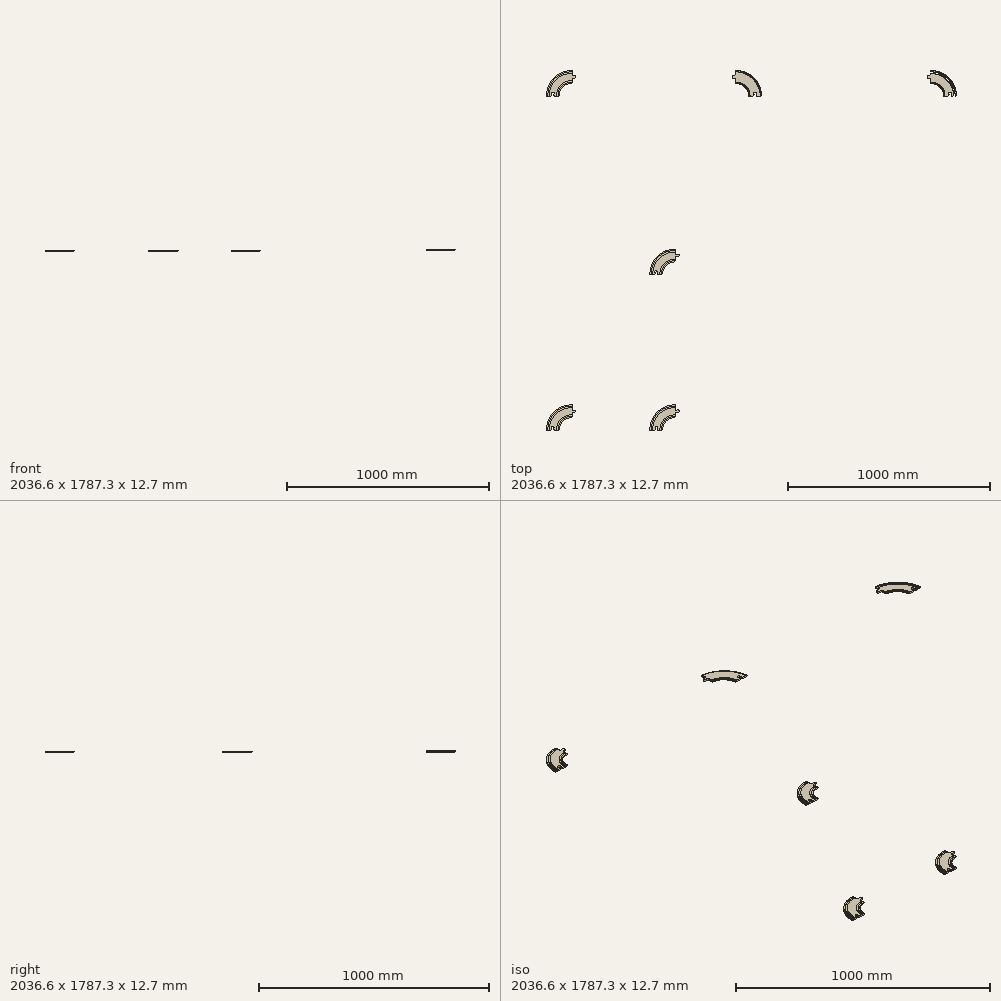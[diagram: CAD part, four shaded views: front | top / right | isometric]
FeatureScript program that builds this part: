
annotation { "Feature Type Name" : "Feature", "Feature Type Description" : "" }
export const myFeature = defineFeature(function(context is Context, id is Id, definition is map)
    precondition{}
    {
        {
            var Q0;
            Q0=qCreatedBy(makeId("Top.planeOp"),FACE);
            var sketch = newSketch(context, id + "F0", { "sketchPlane" : qUnion([Q0])});
            skArc(sketch, "E0", {"start": v(0, 127) * mm, "mid": v(-89.8, 89.8) * mm, "end": v(-127, 0) * mm});
            skArc(sketch, "E1.0", {"start": v(0, 63.5) * mm, "mid": v(-44.9, 44.9) * mm, "end": v(-63.5, 0) * mm});
            skLineSegment(sketch, "E2", {"start": v(-127, 0) * mm, "end": v(-101.6, 0) * mm});
            skLineSegment(sketch, "E3", {"start": v(0, 63.5) * mm, "end": v(0, 88.9) * mm});
            skArc(sketch, "E4", {"start": v(12.7, 88.9) * mm, "mid": v(19.05, 95.25) * mm, "end": v(12.7, 101.6) * mm});
            skPoint(sketch, "E5.start.orphan", {"position": v(12.7, 62.67) * mm});
            skArc(sketch, "E6", {"start": v(12.7, 88.9) * mm, "mid": v(6.35, 90.29) * mm, "end": v(0, 88.9) * mm});
            skArc(sketch, "E7.MirrorCS", {"start": v(12.7, 101.6) * mm, "mid": v(6.35, 100.21) * mm, "end": v(0, 101.6) * mm});
            skArc(sketch, "E8", {"start": v(-88.9, 12.7) * mm, "mid": v(-95.25, 19.05) * mm, "end": v(-101.6, 12.7) * mm});
            skLineSegment(sketch, "E9", {"start": v(-101.6, 12.7) * mm, "end": v(-102.39, 12.7) * mm});
            skPoint(sketch, "E10.startSnap0", {"position": v(-102.39, 12.7) * mm});
            skPoint(sketch, "E11.orphan", {"position": v(-71.93, 12.7) * mm});
            skLineSegment(sketch, "E12.trimOffspring", {"start": v(-126.36, 12.7) * mm, "end": v(-132.85, 12.7) * mm});
            skArc(sketch, "E13", {"start": v(-88.9, 12.7) * mm, "mid": v(-90.29, 6.35) * mm, "end": v(-88.9, 0) * mm});
            skArc(sketch, "E14.MirrorCS", {"start": v(-101.6, 12.7) * mm, "mid": v(-100.21, 6.35) * mm, "end": v(-101.6, 0) * mm});
            skPoint(sketch, "E10.end.orphan", {"position": v(-101.6, 0) * mm});
            skLineSegment(sketch, "E15.trimOffspring", {"start": v(0, 101.6) * mm, "end": v(0, 127) * mm});
            skLineSegment(sketch, "E16.trimOffspring", {"start": v(-88.9, 0) * mm, "end": v(-63.5, 0) * mm});
            skLineSegment(sketch, "E17", {"start": v(76.77, 161.45) * mm, "end": v(76.77, -32.66) * mm});
            skLineSegment(sketch, "E18", {"start": v(333.5, 184.4) * mm, "end": v(333.5, -54.92) * mm});
            skLineSegment(sketch, "E19.MirrorCS", {"start": v(411.86, 12.7) * mm, "end": v(411.07, 12.7) * mm});
            skArc(sketch, "E20.MirrorCS", {"start": v(526.16, 88.9) * mm, "mid": v(519.8, 90.29) * mm, "end": v(513.46, 88.9) * mm});
            skArc(sketch, "E21.MirrorCS", {"start": v(526.16, 101.6) * mm, "mid": v(519.8, 100.21) * mm, "end": v(513.46, 101.6) * mm});
            skArc(sketch, "E22.MirrorCS", {"start": v(411.86, 12.7) * mm, "mid": v(413.24, 6.35) * mm, "end": v(411.86, 0) * mm});
            skArc(sketch, "E23.MirrorCS", {"start": v(424.56, 12.7) * mm, "mid": v(418.2, 19.05) * mm, "end": v(411.86, 12.7) * mm});
            skArc(sketch, "E24.MirrorCS", {"start": v(526.16, 88.9) * mm, "mid": v(532.5, 95.25) * mm, "end": v(526.16, 101.6) * mm});
            skLineSegment(sketch, "E25.MirrorCS", {"start": v(513.46, 63.5) * mm, "end": v(513.46, 88.9) * mm});
            skArc(sketch, "E26.MirrorCS", {"start": v(424.56, 12.7) * mm, "mid": v(423.17, 6.35) * mm, "end": v(424.56, 0) * mm});
            skLineSegment(sketch, "E27.MirrorCS", {"start": v(513.46, 101.6) * mm, "end": v(513.46, 127) * mm});
            skLineSegment(sketch, "E28.MirrorCS", {"start": v(424.56, 0) * mm, "end": v(449.96, 0) * mm});
            skPoint(sketch, "E29.MirrorP", {"position": v(526.16, 62.67) * mm});
            skLineSegment(sketch, "E30.MirrorCS", {"start": v(387.1, 12.7) * mm, "end": v(380.6, 12.7) * mm});
            skLineSegment(sketch, "E31.MirrorCS", {"start": v(386.46, 0) * mm, "end": v(411.86, 0) * mm});
            skPoint(sketch, "E32.MirrorP", {"position": v(411.07, 12.7) * mm});
            skArc(sketch, "E33.MirrorCS", {"start": v(513.46, 127) * mm, "mid": v(423.65, 89.8) * mm, "end": v(386.46, 0) * mm});
            skPoint(sketch, "E34.MirrorP", {"position": v(411.86, 0) * mm});
            skArc(sketch, "E35.MirrorCS", {"start": v(513.46, 63.5) * mm, "mid": v(468.55, 44.9) * mm, "end": v(449.96, 0) * mm});
            skPoint(sketch, "E36.MirrorP", {"position": v(441.53, 12.7) * mm});
            skLineSegment(sketch, "E37.MirrorCS", {"start": v(-101.6, -874.4) * mm, "end": v(-102.39, -874.4) * mm});
            skLineSegment(sketch, "E38.MirrorCS", {"start": v(411.86, -874.4) * mm, "end": v(411.07, -874.4) * mm});
            skArc(sketch, "E39.MirrorCS", {"start": v(424.56, -874.4) * mm, "mid": v(423.17, -880.75) * mm, "end": v(424.56, -887.1) * mm});
            skArc(sketch, "E40.MirrorCS", {"start": v(526.16, -785.5) * mm, "mid": v(519.8, -786.88) * mm, "end": v(513.46, -785.5) * mm});
            skArc(sketch, "E41.MirrorCS", {"start": v(-101.6, -874.4) * mm, "mid": v(-100.21, -880.75) * mm, "end": v(-101.6, -887.1) * mm});
            skArc(sketch, "E42.MirrorCS", {"start": v(424.56, -874.4) * mm, "mid": v(418.2, -868.05) * mm, "end": v(411.86, -874.4) * mm});
            skArc(sketch, "E43.MirrorCS", {"start": v(526.16, -798.2) * mm, "mid": v(519.8, -796.81) * mm, "end": v(513.46, -798.2) * mm});
            skArc(sketch, "E44.MirrorCS", {"start": v(411.86, -874.4) * mm, "mid": v(413.24, -880.75) * mm, "end": v(411.86, -887.1) * mm});
            skArc(sketch, "E45.MirrorCS", {"start": v(-88.9, -874.4) * mm, "mid": v(-90.29, -880.75) * mm, "end": v(-88.9, -887.1) * mm});
            skArc(sketch, "E46.MirrorCS", {"start": v(-88.9, -874.4) * mm, "mid": v(-95.25, -868.05) * mm, "end": v(-101.6, -874.4) * mm});
            skLineSegment(sketch, "E47.MirrorCS", {"start": v(424.56, -887.1) * mm, "end": v(449.96, -887.1) * mm});
            skArc(sketch, "E48.MirrorCS", {"start": v(526.16, -798.2) * mm, "mid": v(532.5, -791.85) * mm, "end": v(526.16, -785.5) * mm});
            skArc(sketch, "E49.MirrorCS", {"start": v(12.7, -798.2) * mm, "mid": v(19.05, -791.85) * mm, "end": v(12.7, -785.5) * mm});
            skArc(sketch, "E50.MirrorCS", {"start": v(12.7, -785.5) * mm, "mid": v(6.35, -786.88) * mm, "end": v(0, -785.5) * mm});
            skArc(sketch, "E51.MirrorCS", {"start": v(12.7, -798.2) * mm, "mid": v(6.35, -796.81) * mm, "end": v(0, -798.2) * mm});
            skLineSegment(sketch, "E52.MirrorCS", {"start": v(-127, -887.1) * mm, "end": v(-101.6, -887.1) * mm});
            skLineSegment(sketch, "E53.MirrorCS", {"start": v(-88.9, -887.1) * mm, "end": v(-63.5, -887.1) * mm});
            skLineSegment(sketch, "E54.MirrorCS", {"start": v(-126.36, -874.4) * mm, "end": v(-132.85, -874.4) * mm});
            skLineSegment(sketch, "E55.MirrorCS", {"start": v(513.46, -823.6) * mm, "end": v(513.46, -798.2) * mm});
            skLineSegment(sketch, "E56.MirrorCS", {"start": v(387.1, -874.4) * mm, "end": v(380.6, -874.4) * mm});
            skLineSegment(sketch, "E57.MirrorCS", {"start": v(513.46, -785.5) * mm, "end": v(513.46, -760.1) * mm});
            skLineSegment(sketch, "E58.MirrorCS", {"start": v(0, -785.5) * mm, "end": v(0, -760.1) * mm});
            skLineSegment(sketch, "E59.MirrorCS", {"start": v(0, -823.6) * mm, "end": v(0, -798.2) * mm});
            skLineSegment(sketch, "E60.MirrorCS", {"start": v(386.46, -887.1) * mm, "end": v(411.86, -887.1) * mm});
            skPoint(sketch, "E61.MirrorP", {"position": v(526.16, -824.42) * mm});
            skPoint(sketch, "E62.MirrorP", {"position": v(-71.93, -874.4) * mm});
            skPoint(sketch, "E63.MirrorP", {"position": v(-101.6, -887.1) * mm});
            skArc(sketch, "E64.MirrorCS", {"start": v(0, -823.6) * mm, "mid": v(-44.9, -842.2) * mm, "end": v(-63.5, -887.1) * mm});
            skLineSegment(sketch, "E65.MirrorCS", {"start": v(333.5, -702.69) * mm, "end": v(333.5, -942.02) * mm});
            skArc(sketch, "E66.MirrorCS", {"start": v(513.46, -823.6) * mm, "mid": v(468.55, -842.2) * mm, "end": v(449.96, -887.1) * mm});
            skArc(sketch, "E67.MirrorCS", {"start": v(513.46, -760.1) * mm, "mid": v(423.65, -797.3) * mm, "end": v(386.46, -887.1) * mm});
            skPoint(sketch, "E68.MirrorP", {"position": v(411.86, -887.1) * mm});
            skPoint(sketch, "E69.MirrorP", {"position": v(441.53, -874.4) * mm});
            skArc(sketch, "E70.MirrorCS", {"start": v(0, -760.1) * mm, "mid": v(-89.8, -797.3) * mm, "end": v(-127, -887.1) * mm});
            skPoint(sketch, "E71.MirrorP", {"position": v(12.7, -824.42) * mm});
            skPoint(sketch, "E72.MirrorP", {"position": v(-102.39, -874.4) * mm});
            skLineSegment(sketch, "E73.MirrorCS", {"start": v(76.77, -725.65) * mm, "end": v(76.77, -919.76) * mm});
            skPoint(sketch, "E74.MirrorP", {"position": v(411.07, -874.4) * mm});
            skLineSegment(sketch, "E75.MirrorCS", {"start": v(411.86, -1647.6) * mm, "end": v(411.07, -1647.6) * mm});
            skArc(sketch, "E76.MirrorCS", {"start": v(424.56, -1647.6) * mm, "mid": v(418.2, -1641.26) * mm, "end": v(411.86, -1647.6) * mm});
            skArc(sketch, "E77.MirrorCS", {"start": v(424.56, -1647.6) * mm, "mid": v(423.17, -1653.96) * mm, "end": v(424.56, -1660.3) * mm});
            skArc(sketch, "E78.MirrorCS", {"start": v(411.86, -1647.6) * mm, "mid": v(413.24, -1653.96) * mm, "end": v(411.86, -1660.3) * mm});
            skLineSegment(sketch, "E79.MirrorCS", {"start": v(386.46, -1660.3) * mm, "end": v(411.86, -1660.3) * mm});
            skArc(sketch, "E80.MirrorCS", {"start": v(-88.9, -1647.6) * mm, "mid": v(-90.29, -1653.96) * mm, "end": v(-88.9, -1660.3) * mm});
            skLineSegment(sketch, "E81.MirrorCS", {"start": v(-127, -1660.3) * mm, "end": v(-101.6, -1660.3) * mm});
            skLineSegment(sketch, "E82.MirrorCS", {"start": v(-101.6, -1647.6) * mm, "end": v(-102.39, -1647.6) * mm});
            skArc(sketch, "E83.MirrorCS", {"start": v(-101.6, -1647.6) * mm, "mid": v(-100.21, -1653.96) * mm, "end": v(-101.6, -1660.3) * mm});
            skArc(sketch, "E84.MirrorCS", {"start": v(-88.9, -1647.6) * mm, "mid": v(-95.25, -1641.26) * mm, "end": v(-101.6, -1647.6) * mm});
            skArc(sketch, "E85.MirrorCS", {"start": v(526.16, -1571.4) * mm, "mid": v(519.8, -1570.02) * mm, "end": v(513.46, -1571.4) * mm});
            skArc(sketch, "E86.MirrorCS", {"start": v(526.16, -1558.7) * mm, "mid": v(519.8, -1560.1) * mm, "end": v(513.46, -1558.7) * mm});
            skLineSegment(sketch, "E87.MirrorCS", {"start": v(513.46, -1596.8) * mm, "end": v(513.46, -1571.4) * mm});
            skArc(sketch, "E88.MirrorCS", {"start": v(526.16, -1571.4) * mm, "mid": v(532.5, -1565.06) * mm, "end": v(526.16, -1558.7) * mm});
            skArc(sketch, "E89.MirrorCS", {"start": v(12.7, -1571.4) * mm, "mid": v(19.05, -1565.06) * mm, "end": v(12.7, -1558.7) * mm});
            skArc(sketch, "E90.MirrorCS", {"start": v(12.7, -1571.4) * mm, "mid": v(6.35, -1570.02) * mm, "end": v(0, -1571.4) * mm});
            skArc(sketch, "E91.MirrorCS", {"start": v(12.7, -1558.7) * mm, "mid": v(6.35, -1560.1) * mm, "end": v(0, -1558.7) * mm});
            skLineSegment(sketch, "E92.MirrorCS", {"start": v(-88.9, -1660.3) * mm, "end": v(-63.5, -1660.3) * mm});
            skLineSegment(sketch, "E93.MirrorCS", {"start": v(424.56, -1660.3) * mm, "end": v(449.96, -1660.3) * mm});
            skLineSegment(sketch, "E94.MirrorCS", {"start": v(513.46, -1558.7) * mm, "end": v(513.46, -1533.3) * mm});
            skLineSegment(sketch, "E95.MirrorCS", {"start": v(0, -1596.8) * mm, "end": v(0, -1571.4) * mm});
            skLineSegment(sketch, "E96.MirrorCS", {"start": v(-126.36, -1647.6) * mm, "end": v(-132.85, -1647.6) * mm});
            skLineSegment(sketch, "E97.MirrorCS", {"start": v(387.1, -1647.6) * mm, "end": v(380.6, -1647.6) * mm});
            skLineSegment(sketch, "E98.MirrorCS", {"start": v(0, -1558.7) * mm, "end": v(0, -1533.3) * mm});
            skPoint(sketch, "E99.MirrorP", {"position": v(526.16, -1597.64) * mm});
            skArc(sketch, "E100.MirrorCS", {"start": v(0, -1533.3) * mm, "mid": v(-89.8, -1570.5) * mm, "end": v(-127, -1660.3) * mm});
            skPoint(sketch, "E101.MirrorP", {"position": v(441.53, -1647.6) * mm});
            skArc(sketch, "E102.MirrorCS", {"start": v(513.46, -1596.8) * mm, "mid": v(468.55, -1615.4) * mm, "end": v(449.96, -1660.3) * mm});
            skPoint(sketch, "E103.MirrorP", {"position": v(411.07, -1647.6) * mm});
            skPoint(sketch, "E104.MirrorP", {"position": v(411.86, -1660.3) * mm});
            skPoint(sketch, "E105.MirrorP", {"position": v(-71.93, -1647.6) * mm});
            skPoint(sketch, "E106.MirrorP", {"position": v(-102.39, -1647.6) * mm});
            skLineSegment(sketch, "E107.MirrorCS", {"start": v(333.5, -1475.9) * mm, "end": v(333.5, -1715.23) * mm});
            skPoint(sketch, "E108.MirrorP", {"position": v(-101.6, -1660.3) * mm});
            skArc(sketch, "E109.MirrorCS", {"start": v(513.46, -1533.3) * mm, "mid": v(423.65, -1570.5) * mm, "end": v(386.46, -1660.3) * mm});
            skLineSegment(sketch, "E110.MirrorCS", {"start": v(76.77, -1498.86) * mm, "end": v(76.77, -1692.97) * mm});
            skPoint(sketch, "E111.MirrorP", {"position": v(12.7, -1597.64) * mm});
            skArc(sketch, "E112.MirrorCS", {"start": v(0, -1596.8) * mm, "mid": v(-44.9, -1615.4) * mm, "end": v(-63.5, -1660.3) * mm});
            skLineSegment(sketch, "E113", {"start": v(663.76, 185.94) * mm, "end": v(663.76, -109.84) * mm});
            skLineSegment(sketch, "E114", {"start": v(308.83, -128.2) * mm, "end": v(873.87, -128.2) * mm});
            skArc(sketch, "E115.MirrorCS", {"start": v(915.67, 12.7) * mm, "mid": v(914.28, 6.35) * mm, "end": v(915.67, 0) * mm});
            skArc(sketch, "E116.MirrorCS", {"start": v(902.97, 12.7) * mm, "mid": v(909.32, 19.05) * mm, "end": v(915.67, 12.7) * mm});
            skArc(sketch, "E117.MirrorCS", {"start": v(902.97, 12.7) * mm, "mid": v(904.35, 6.35) * mm, "end": v(902.97, 0) * mm});
            skLineSegment(sketch, "E118.MirrorCS", {"start": v(915.67, 12.7) * mm, "end": v(916.46, 12.7) * mm});
            skArc(sketch, "E119.MirrorCS", {"start": v(801.37, 88.9) * mm, "mid": v(807.72, 90.29) * mm, "end": v(814.07, 88.9) * mm});
            skArc(sketch, "E120.MirrorCS", {"start": v(801.37, 101.6) * mm, "mid": v(807.72, 100.21) * mm, "end": v(814.07, 101.6) * mm});
            skLineSegment(sketch, "E121.MirrorCS", {"start": v(814.07, 63.5) * mm, "end": v(814.07, 88.9) * mm});
            skArc(sketch, "E122.MirrorCS", {"start": v(801.37, 88.9) * mm, "mid": v(795.02, 95.25) * mm, "end": v(801.37, 101.6) * mm});
            skLineSegment(sketch, "E123.MirrorCS", {"start": v(814.07, 101.6) * mm, "end": v(814.07, 127) * mm});
            skLineSegment(sketch, "E124.MirrorCS", {"start": v(941.07, 0) * mm, "end": v(915.67, 0) * mm});
            skLineSegment(sketch, "E125.MirrorCS", {"start": v(902.97, 0) * mm, "end": v(877.57, 0) * mm});
            skLineSegment(sketch, "E126.MirrorCS", {"start": v(940.43, 12.7) * mm, "end": v(946.92, 12.7) * mm});
            skPoint(sketch, "E127.MirrorP", {"position": v(801.37, 62.67) * mm});
            skPoint(sketch, "E128.MirrorP", {"position": v(916.46, 12.7) * mm});
            skArc(sketch, "E129.MirrorCS", {"start": v(814.07, 63.5) * mm, "mid": v(858.97, 44.9) * mm, "end": v(877.57, 0) * mm});
            skArc(sketch, "E130.MirrorCS", {"start": v(814.07, 127) * mm, "mid": v(903.87, 89.8) * mm, "end": v(941.07, 0) * mm});
            skPoint(sketch, "E131.MirrorP", {"position": v(915.67, 0) * mm});
            skPoint(sketch, "E132.MirrorP", {"position": v(886, 12.7) * mm});
            skArc(sketch, "E133.MirrorCS", {"start": v(424.56, -269.1) * mm, "mid": v(423.17, -262.75) * mm, "end": v(424.56, -256.4) * mm});
            skArc(sketch, "E134.MirrorCS", {"start": v(526.16, -345.3) * mm, "mid": v(519.8, -346.68) * mm, "end": v(513.46, -345.3) * mm});
            skArc(sketch, "E135.MirrorCS", {"start": v(411.86, -269.1) * mm, "mid": v(413.24, -262.75) * mm, "end": v(411.86, -256.4) * mm});
            skLineSegment(sketch, "E136.MirrorCS", {"start": v(411.86, -269.1) * mm, "end": v(411.07, -269.1) * mm});
            skArc(sketch, "E137.MirrorCS", {"start": v(526.16, -358) * mm, "mid": v(519.8, -356.61) * mm, "end": v(513.46, -358) * mm});
            skArc(sketch, "E138.MirrorCS", {"start": v(424.56, -269.1) * mm, "mid": v(418.2, -275.45) * mm, "end": v(411.86, -269.1) * mm});
            skArc(sketch, "E139.MirrorCS", {"start": v(526.16, -345.3) * mm, "mid": v(532.5, -351.65) * mm, "end": v(526.16, -358) * mm});
            skLineSegment(sketch, "E140.MirrorCS", {"start": v(424.56, -256.4) * mm, "end": v(449.96, -256.4) * mm});
            skLineSegment(sketch, "E141.MirrorCS", {"start": v(513.46, -319.9) * mm, "end": v(513.46, -345.3) * mm});
            skLineSegment(sketch, "E142.MirrorCS", {"start": v(387.1, -269.1) * mm, "end": v(380.6, -269.1) * mm});
            skLineSegment(sketch, "E143.MirrorCS", {"start": v(386.46, -256.4) * mm, "end": v(411.86, -256.4) * mm});
            skLineSegment(sketch, "E144.MirrorCS", {"start": v(513.46, -358) * mm, "end": v(513.46, -383.4) * mm});
            skPoint(sketch, "E145.MirrorP", {"position": v(526.16, -319.07) * mm});
            skArc(sketch, "E146.MirrorCS", {"start": v(513.46, -383.4) * mm, "mid": v(423.65, -346.2) * mm, "end": v(386.46, -256.4) * mm});
            skArc(sketch, "E147.MirrorCS", {"start": v(513.46, -319.9) * mm, "mid": v(468.55, -301.3) * mm, "end": v(449.96, -256.4) * mm});
            skPoint(sketch, "E148.MirrorP", {"position": v(411.86, -256.4) * mm});
            skPoint(sketch, "E149.MirrorP", {"position": v(441.53, -269.1) * mm});
            skPoint(sketch, "E150.MirrorP", {"position": v(411.07, -269.1) * mm});
            skSolve(sketch);
        }
        {
            var Q0;
            Q0=makeQuery(id+"F0.imprint","IMPRINT",FACE,{"disambiguationData":[TD([[makeQuery(id+"F0.imprint","IMPRINT",EDGE,{"derivedFrom":sQuery(id+"F0.wireOp",EDGE,"E1.0")}),-1.0]])]});
            var Q1;
            Q1=makeQuery(id+"F0.imprint","IMPRINT",FACE,{"disambiguationData":[TD([[makeQuery(id+"F0.imprint","IMPRINT",EDGE,{"derivedFrom":sQuery(id+"F0.wireOp",EDGE,"E22.MirrorCS")}),-1.0]])]});
            var Q2;
            Q2=makeQuery(id+"F0.imprint","IMPRINT",FACE,{"disambiguationData":[TD([[makeQuery(id+"F0.imprint","IMPRINT",EDGE,{"derivedFrom":sQuery(id+"F0.wireOp",EDGE,"E39.MirrorCS")}),1.0]])]});
            var Q3;
            Q3=makeQuery(id+"F0.imprint","IMPRINT",FACE,{"disambiguationData":[TD([[makeQuery(id+"F0.imprint","IMPRINT",EDGE,{"derivedFrom":sQuery(id+"F0.wireOp",EDGE,"E41.MirrorCS")}),-1.0]])]});
            var Q4;
            Q4=makeQuery(id+"F0.imprint","IMPRINT",FACE,{"disambiguationData":[TD([[makeQuery(id+"F0.imprint","IMPRINT",EDGE,{"derivedFrom":sQuery(id+"F0.wireOp",EDGE,"E80.MirrorCS")}),1.0]])]});
            var Q5;
            Q5=makeQuery(id+"F0.imprint","IMPRINT",FACE,{"disambiguationData":[TD([[makeQuery(id+"F0.imprint","IMPRINT",EDGE,{"derivedFrom":sQuery(id+"F0.wireOp",EDGE,"E115.MirrorCS")}),1.0]])]});
            var Q6;
            Q6=makeQuery(id+"F0.imprint","IMPRINT",FACE,{"disambiguationData":[TD([[makeQuery(id+"F0.imprint","IMPRINT",EDGE,{"derivedFrom":sQuery(id+"F0.wireOp",EDGE,"E133.MirrorCS")}),-1.0]])]});
            var Q7;
            Q7=makeQuery(id+"F0.imprint","IMPRINT",FACE,{"disambiguationData":[TD([[makeQuery(id+"F0.imprint","IMPRINT",EDGE,{"derivedFrom":sQuery(id+"F0.wireOp",EDGE,"E76.MirrorCS")}),-1.0]])]});
            extrude(context, id + "F1", {"entities" : qUnion([Q0, Q1, Q2, Q3, Q4, Q5, Q6, Q7]), "depth" : 6.35 * mm});
        }
        {
            var Q0;
            Q0=makeQuery(id+"F1.opExtrude","CAP_FACE",FACE,{"disambiguationData":[OSD([sQuery(id+"F0.wireOp",EDGE,"E0"),sQuery(id+"F0.wireOp",EDGE,"E1.0"),sQuery(id+"F0.wireOp",EDGE,"E2"),sQuery(id+"F0.wireOp",EDGE,"E3"),sQuery(id+"F0.wireOp",EDGE,"E4"),sQuery(id+"F0.wireOp",EDGE,"E6"),sQuery(id+"F0.wireOp",EDGE,"E7.MirrorCS"),sQuery(id+"F0.wireOp",EDGE,"E8"),sQuery(id+"F0.wireOp",EDGE,"E13"),sQuery(id+"F0.wireOp",EDGE,"E14.MirrorCS"),sQuery(id+"F0.wireOp",EDGE,"E15.trimOffspring"),sQuery(id+"F0.wireOp",EDGE,"E16.trimOffspring")])],"isStart":false});
            var sketch = newSketch(context, id + "F2", { "sketchPlane" : qUnion([Q0])});
            skArc(sketch, "E151.0", {"start": v(0, 63.5) * mm, "mid": v(-44.9, 44.9) * mm, "end": v(-63.5, 0) * mm});
            skArc(sketch, "E151.1", {"start": v(0, 127) * mm, "mid": v(-89.8, 89.8) * mm, "end": v(-127, 0) * mm});
            skLineSegment(sketch, "E152.0", {"start": v(76.77, 161.45) * mm, "end": v(76.77, -32.66) * mm});
            skLineSegment(sketch, "E152.1", {"start": v(333.5, 184.4) * mm, "end": v(333.5, -54.92) * mm});
            skArc(sketch, "E153.0", {"start": v(0, 69.85) * mm, "mid": v(-49.4, 49.4) * mm, "end": v(-69.85, 0) * mm});
            skArc(sketch, "E154.0", {"start": v(0, 77.47) * mm, "mid": v(-54.78, 54.78) * mm, "end": v(-77.47, 0) * mm});
            skArc(sketch, "E155.0", {"start": v(0, 120.65) * mm, "mid": v(-85.31, 85.31) * mm, "end": v(-120.65, 0) * mm});
            skArc(sketch, "E156.0", {"start": v(0, 113.03) * mm, "mid": v(-79.92, 79.92) * mm, "end": v(-113.03, 0) * mm});
            skArc(sketch, "E157.MirrorCS", {"start": v(153.53, 113.03) * mm, "mid": v(233.46, 79.92) * mm, "end": v(266.56, 0) * mm});
            skArc(sketch, "E158.MirrorCS", {"start": v(153.53, 120.65) * mm, "mid": v(238.85, 85.31) * mm, "end": v(274.18, 0) * mm});
            skArc(sketch, "E159.MirrorCS", {"start": v(153.53, 69.85) * mm, "mid": v(202.93, 49.4) * mm, "end": v(223.38, 0) * mm});
            skArc(sketch, "E160.MirrorCS", {"start": v(153.53, 77.47) * mm, "mid": v(208.31, 54.78) * mm, "end": v(231, 0) * mm});
            skArc(sketch, "E161.MirrorCS", {"start": v(513.46, 120.65) * mm, "mid": v(428.14, 85.31) * mm, "end": v(392.8, 0) * mm});
            skArc(sketch, "E162.MirrorCS", {"start": v(513.46, 113.03) * mm, "mid": v(433.53, 79.92) * mm, "end": v(400.43, 0) * mm});
            skArc(sketch, "E163.MirrorCS", {"start": v(513.46, 69.85) * mm, "mid": v(464.06, 49.4) * mm, "end": v(443.6, 0) * mm});
            skArc(sketch, "E164.MirrorCS", {"start": v(513.46, 77.47) * mm, "mid": v(458.68, 54.78) * mm, "end": v(435.99, 0) * mm});
            skArc(sketch, "E165.MirrorCS", {"start": v(0, -403.9) * mm, "mid": v(-54.78, -381.21) * mm, "end": v(-77.47, -326.43) * mm});
            skArc(sketch, "E166.MirrorCS", {"start": v(0, -396.28) * mm, "mid": v(-49.4, -375.82) * mm, "end": v(-69.85, -326.43) * mm});
            skArc(sketch, "E167.MirrorCS", {"start": v(0, -447.08) * mm, "mid": v(-85.31, -411.74) * mm, "end": v(-120.65, -326.43) * mm});
            skLineSegment(sketch, "E168.MirrorCS", {"start": v(333.5, -510.84) * mm, "end": v(333.5, -271.5) * mm});
            skArc(sketch, "E169.MirrorCS", {"start": v(0, -439.46) * mm, "mid": v(-79.92, -406.36) * mm, "end": v(-113.03, -326.43) * mm});
            skArc(sketch, "E170.MirrorCS", {"start": v(153.53, -439.46) * mm, "mid": v(233.46, -406.36) * mm, "end": v(266.56, -326.43) * mm});
            skLineSegment(sketch, "E171.MirrorCS", {"start": v(76.77, -487.88) * mm, "end": v(76.77, -293.77) * mm});
            skArc(sketch, "E172.MirrorCS", {"start": v(0, -453.43) * mm, "mid": v(-89.8, -416.23) * mm, "end": v(-127, -326.43) * mm});
            skArc(sketch, "E173.MirrorCS", {"start": v(153.53, -447.08) * mm, "mid": v(238.85, -411.74) * mm, "end": v(274.18, -326.43) * mm});
            skArc(sketch, "E174.MirrorCS", {"start": v(0, -389.93) * mm, "mid": v(-44.9, -371.33) * mm, "end": v(-63.5, -326.43) * mm});
            skArc(sketch, "E175.MirrorCS", {"start": v(513.46, -396.28) * mm, "mid": v(464.06, -375.82) * mm, "end": v(443.6, -326.43) * mm});
            skArc(sketch, "E176.MirrorCS", {"start": v(153.53, -396.28) * mm, "mid": v(202.93, -375.82) * mm, "end": v(223.38, -326.43) * mm});
            skArc(sketch, "E177.MirrorCS", {"start": v(153.53, -403.9) * mm, "mid": v(208.31, -381.21) * mm, "end": v(231, -326.43) * mm});
            skArc(sketch, "E178.MirrorCS", {"start": v(513.46, -439.46) * mm, "mid": v(433.53, -406.36) * mm, "end": v(400.43, -326.43) * mm});
            skArc(sketch, "E179.MirrorCS", {"start": v(513.46, -447.08) * mm, "mid": v(428.14, -411.74) * mm, "end": v(392.8, -326.43) * mm});
            skArc(sketch, "E180.MirrorCS", {"start": v(513.46, -403.9) * mm, "mid": v(458.68, -381.21) * mm, "end": v(435.99, -326.43) * mm});
            skLineSegment(sketch, "E181", {"start": v(-77.47, 0) * mm, "end": v(-69.85, 0) * mm});
            skLineSegment(sketch, "E182", {"start": v(-113.03, 0) * mm, "end": v(-120.65, 0) * mm});
            skLineSegment(sketch, "E183", {"start": v(0, 69.85) * mm, "end": v(0, 77.47) * mm});
            skLineSegment(sketch, "E184", {"start": v(0, 113.03) * mm, "end": v(0, 120.65) * mm});
            skLineSegment(sketch, "E185", {"start": v(153.53, 77.47) * mm, "end": v(153.53, 69.85) * mm});
            skLineSegment(sketch, "E186", {"start": v(153.53, 113.03) * mm, "end": v(153.53, 120.65) * mm});
            skLineSegment(sketch, "E187", {"start": v(223.38, 0) * mm, "end": v(231, 0) * mm});
            skLineSegment(sketch, "E188", {"start": v(266.56, 0) * mm, "end": v(274.18, 0) * mm});
            skLineSegment(sketch, "E189", {"start": v(392.8, 0) * mm, "end": v(400.43, 0) * mm});
            skLineSegment(sketch, "E190", {"start": v(435.99, 0) * mm, "end": v(443.6, 0) * mm});
            skLineSegment(sketch, "E191", {"start": v(513.46, 69.85) * mm, "end": v(513.46, 77.47) * mm});
            skLineSegment(sketch, "E192", {"start": v(513.46, 120.65) * mm, "end": v(513.46, 113.03) * mm});
            skLineSegment(sketch, "E193", {"start": v(392.8, -326.43) * mm, "end": v(400.43, -326.43) * mm});
            skLineSegment(sketch, "E194", {"start": v(435.99, -326.43) * mm, "end": v(443.6, -326.43) * mm});
            skLineSegment(sketch, "E195", {"start": v(513.46, -396.28) * mm, "end": v(513.46, -403.9) * mm});
            skLineSegment(sketch, "E196", {"start": v(513.46, -447.08) * mm, "end": v(513.46, -439.46) * mm});
            skLineSegment(sketch, "E197", {"start": v(266.56, -326.43) * mm, "end": v(274.18, -326.43) * mm});
            skLineSegment(sketch, "E198", {"start": v(231, -326.43) * mm, "end": v(223.38, -326.43) * mm});
            skLineSegment(sketch, "E199", {"start": v(153.53, -396.28) * mm, "end": v(153.53, -403.9) * mm});
            skLineSegment(sketch, "E200", {"start": v(153.53, -439.46) * mm, "end": v(153.53, -447.08) * mm});
            skLineSegment(sketch, "E201", {"start": v(0, -403.9) * mm, "end": v(0, -396.28) * mm});
            skLineSegment(sketch, "E202", {"start": v(0, -447.08) * mm, "end": v(0, -439.46) * mm});
            skLineSegment(sketch, "E203", {"start": v(-69.85, -326.43) * mm, "end": v(-77.47, -326.43) * mm});
            skLineSegment(sketch, "E204", {"start": v(-113.03, -326.43) * mm, "end": v(-120.65, -326.43) * mm});
            skArc(sketch, "E205.0", {"start": v(0, -760.1) * mm, "mid": v(-89.8, -797.3) * mm, "end": v(-127, -887.1) * mm});
            skArc(sketch, "E205.1", {"start": v(0, -823.6) * mm, "mid": v(-44.9, -842.2) * mm, "end": v(-63.5, -887.1) * mm});
            skArc(sketch, "E205.2", {"start": v(513.46, -760.1) * mm, "mid": v(423.65, -797.3) * mm, "end": v(386.46, -887.1) * mm});
            skArc(sketch, "E205.3", {"start": v(513.46, -823.6) * mm, "mid": v(468.55, -842.2) * mm, "end": v(449.96, -887.1) * mm});
            skPoint(sketch, "E206.endSnap0", {"position": v(0, -606.77) * mm});
            skLineSegment(sketch, "E207.MirrorCS", {"start": v(0, -766.45) * mm, "end": v(0, -774.07) * mm});
            skLineSegment(sketch, "E208.MirrorCS", {"start": v(392.8, -887.1) * mm, "end": v(400.43, -887.1) * mm});
            skLineSegment(sketch, "E209.MirrorCS", {"start": v(0, -809.63) * mm, "end": v(0, -817.25) * mm});
            skLineSegment(sketch, "E210.MirrorCS", {"start": v(435.99, -887.1) * mm, "end": v(443.6, -887.1) * mm});
            skLineSegment(sketch, "E211.MirrorCS", {"start": v(513.46, -817.25) * mm, "end": v(513.46, -809.63) * mm});
            skLineSegment(sketch, "E212.MirrorCS", {"start": v(513.46, -766.45) * mm, "end": v(513.46, -774.07) * mm});
            skLineSegment(sketch, "E213.MirrorCS", {"start": v(-69.85, -887.1) * mm, "end": v(-77.47, -887.1) * mm});
            skLineSegment(sketch, "E214.MirrorCS", {"start": v(231, -887.1) * mm, "end": v(223.38, -887.1) * mm});
            skLineSegment(sketch, "E215.MirrorCS", {"start": v(153.53, -774.07) * mm, "end": v(153.53, -766.45) * mm});
            skLineSegment(sketch, "E216.MirrorCS", {"start": v(153.53, -817.25) * mm, "end": v(153.53, -809.63) * mm});
            skLineSegment(sketch, "E217.MirrorCS", {"start": v(266.56, -887.1) * mm, "end": v(274.18, -887.1) * mm});
            skLineSegment(sketch, "E218.MirrorCS", {"start": v(-113.03, -887.1) * mm, "end": v(-120.65, -887.1) * mm});
            skLineSegment(sketch, "E219.MirrorCS", {"start": v(333.5, -702.69) * mm, "end": v(333.5, -942.02) * mm});
            skLineSegment(sketch, "E220.MirrorCS", {"start": v(0, -760.1) * mm, "end": v(0, -453.43) * mm});
            skArc(sketch, "E221.MirrorCS", {"start": v(0, -774.07) * mm, "mid": v(-79.92, -807.17) * mm, "end": v(-113.03, -887.1) * mm});
            skArc(sketch, "E222.MirrorCS", {"start": v(513.46, -766.45) * mm, "mid": v(428.14, -801.79) * mm, "end": v(392.8, -887.1) * mm});
            skArc(sketch, "E223.MirrorCS", {"start": v(153.53, -774.07) * mm, "mid": v(233.46, -807.17) * mm, "end": v(266.56, -887.1) * mm});
            skLineSegment(sketch, "E224.MirrorCS", {"start": v(76.77, -725.65) * mm, "end": v(76.77, -919.76) * mm});
            skArc(sketch, "E225.MirrorCS", {"start": v(153.53, -766.45) * mm, "mid": v(238.85, -801.79) * mm, "end": v(274.18, -887.1) * mm});
            skArc(sketch, "E226.MirrorCS", {"start": v(153.53, -809.63) * mm, "mid": v(208.31, -832.32) * mm, "end": v(231, -887.1) * mm});
            skArc(sketch, "E227.MirrorCS", {"start": v(513.46, -817.25) * mm, "mid": v(464.06, -837.7) * mm, "end": v(443.6, -887.1) * mm});
            skArc(sketch, "E228.MirrorCS", {"start": v(0, -766.45) * mm, "mid": v(-85.31, -801.79) * mm, "end": v(-120.65, -887.1) * mm});
            skArc(sketch, "E229.MirrorCS", {"start": v(0, -817.25) * mm, "mid": v(-49.4, -837.7) * mm, "end": v(-69.85, -887.1) * mm});
            skArc(sketch, "E230.MirrorCS", {"start": v(0, -809.63) * mm, "mid": v(-54.78, -832.32) * mm, "end": v(-77.47, -887.1) * mm});
            skArc(sketch, "E231.MirrorCS", {"start": v(513.46, -809.63) * mm, "mid": v(458.68, -832.32) * mm, "end": v(435.99, -887.1) * mm});
            skArc(sketch, "E232.MirrorCS", {"start": v(513.46, -774.07) * mm, "mid": v(433.53, -807.17) * mm, "end": v(400.43, -887.1) * mm});
            skArc(sketch, "E233.MirrorCS", {"start": v(153.53, -817.25) * mm, "mid": v(202.93, -837.7) * mm, "end": v(223.38, -887.1) * mm});
            skArc(sketch, "E234.0", {"start": v(0, -1533.3) * mm, "mid": v(-89.8, -1570.5) * mm, "end": v(-127, -1660.3) * mm});
            skArc(sketch, "E235.0", {"start": v(0, -1590.46) * mm, "mid": v(-49.4, -1610.92) * mm, "end": v(-69.85, -1660.3) * mm});
            skArc(sketch, "E236.0", {"start": v(0, -1582.84) * mm, "mid": v(-54.78, -1605.53) * mm, "end": v(-77.47, -1660.3) * mm});
            skArc(sketch, "E237.0", {"start": v(513.46, -1533.3) * mm, "mid": v(423.65, -1570.5) * mm, "end": v(386.46, -1660.3) * mm});
            skArc(sketch, "E238.0", {"start": v(513.46, -1590.46) * mm, "mid": v(464.06, -1610.92) * mm, "end": v(443.6, -1660.3) * mm});
            skArc(sketch, "E239.0", {"start": v(513.46, -1582.84) * mm, "mid": v(458.68, -1605.53) * mm, "end": v(435.99, -1660.3) * mm});
            skArc(sketch, "E240.0", {"start": v(513.46, -1539.66) * mm, "mid": v(428.14, -1575) * mm, "end": v(392.8, -1660.3) * mm});
            skArc(sketch, "E241.0", {"start": v(513.46, -1547.28) * mm, "mid": v(433.53, -1580.39) * mm, "end": v(400.43, -1660.3) * mm});
            skLineSegment(sketch, "E242.0", {"start": v(0, -1660.3) * mm, "end": v(0, -1660.3) * mm});
            skArc(sketch, "E243.0", {"start": v(0, -1539.66) * mm, "mid": v(-85.31, -1575) * mm, "end": v(-120.65, -1660.3) * mm});
            skArc(sketch, "E244.0", {"start": v(0, -1547.28) * mm, "mid": v(-79.92, -1580.39) * mm, "end": v(-113.03, -1660.3) * mm});
            skLineSegment(sketch, "E245", {"start": v(0, -1547.28) * mm, "end": v(0, -1539.66) * mm});
            skLineSegment(sketch, "E246", {"start": v(-77.47, -1660.3) * mm, "end": v(-69.85, -1660.3) * mm});
            skLineSegment(sketch, "E247", {"start": v(-113.03, -1660.3) * mm, "end": v(-120.65, -1660.3) * mm});
            skLineSegment(sketch, "E248", {"start": v(0, -1590.46) * mm, "end": v(0, -1582.84) * mm});
            skLineSegment(sketch, "E249", {"start": v(400.43, -1660.3) * mm, "end": v(392.8, -1660.3) * mm});
            skLineSegment(sketch, "E250", {"start": v(435.99, -1660.3) * mm, "end": v(443.6, -1660.3) * mm});
            skLineSegment(sketch, "E251", {"start": v(513.46, -1590.46) * mm, "end": v(513.46, -1582.84) * mm});
            skLineSegment(sketch, "E252", {"start": v(513.46, -1547.28) * mm, "end": v(513.46, -1539.66) * mm});
            skSolve(sketch);
        }
        {
            var Q0;
            Q0 = qSketchRegion(id + "F2", true);
            extrude(context, id + "F3", {"entities" : qUnion([Q0]), "operationType" : NewBodyOperationType.REMOVE, "oppositeDirection" : true, "depth" : 1.9 * mm});
        }
        {
            var Q0;
            Q0=makeQuery(id+"F1.opExtrude","CAP_FACE",FACE,{"disambiguationData":[OSD([sQuery(id+"F0.wireOp",EDGE,"E115.MirrorCS"),sQuery(id+"F0.wireOp",EDGE,"E116.MirrorCS"),sQuery(id+"F0.wireOp",EDGE,"E117.MirrorCS"),sQuery(id+"F0.wireOp",EDGE,"E121.MirrorCS"),sQuery(id+"F0.wireOp",EDGE,"E120.MirrorCS"),sQuery(id+"F0.wireOp",EDGE,"E122.MirrorCS"),sQuery(id+"F0.wireOp",EDGE,"E119.MirrorCS"),sQuery(id+"F0.wireOp",EDGE,"E123.MirrorCS"),sQuery(id+"F0.wireOp",EDGE,"E124.MirrorCS"),sQuery(id+"F0.wireOp",EDGE,"E125.MirrorCS"),sQuery(id+"F0.wireOp",EDGE,"E129.MirrorCS"),sQuery(id+"F0.wireOp",EDGE,"E130.MirrorCS")])],"isStart":false});
            var sketch = newSketch(context, id + "F4", { "sketchPlane" : qUnion([Q0])});
            skArc(sketch, "E253.0", {"start": v(814.07, 69.85) * mm, "mid": v(863.46, 49.4) * mm, "end": v(883.92, 0) * mm});
            skArc(sketch, "E254.0", {"start": v(814.07, 77.47) * mm, "mid": v(868.85, 54.78) * mm, "end": v(891.54, 0) * mm});
            skArc(sketch, "E255.0", {"start": v(814.07, 120.65) * mm, "mid": v(899.38, 85.31) * mm, "end": v(934.72, 0) * mm});
            skArc(sketch, "E256.0", {"start": v(814.07, 113.03) * mm, "mid": v(894, 79.92) * mm, "end": v(927.1, 0) * mm});
            skLineSegment(sketch, "E257", {"start": v(814.07, 120.65) * mm, "end": v(814.07, 113.03) * mm});
            skLineSegment(sketch, "E258", {"start": v(814.07, 77.47) * mm, "end": v(814.07, 69.85) * mm});
            skLineSegment(sketch, "E259", {"start": v(891.54, 0) * mm, "end": v(883.92, 0) * mm});
            skLineSegment(sketch, "E260", {"start": v(927.1, 0) * mm, "end": v(934.72, 0) * mm});
            skSolve(sketch);
        }
        {
            var Q0;
            Q0=makeQuery(id+"F4.imprint","IMPRINT",FACE,{"disambiguationData":[TD([[makeQuery(id+"F4.imprint","IMPRINT",EDGE,{"derivedFrom":sQuery(id+"F4.wireOp",EDGE,"E255.0")}),-1.0]])]});
            var Q1;
            Q1=makeQuery(id+"F4.imprint","IMPRINT",FACE,{"disambiguationData":[TD([[makeQuery(id+"F4.imprint","IMPRINT",EDGE,{"derivedFrom":sQuery(id+"F4.wireOp",EDGE,"E253.0")}),1.0]])]});
            extrude(context, id + "F5", {"entities" : qUnion([Q0, Q1]), "operationType" : NewBodyOperationType.REMOVE, "oppositeDirection" : true, "depth" : 1.9 * mm});
        }
        {
            var Q0;
            {var subQ0=sQuery(id+"F0.wireOp",EDGE,"E125.MirrorCS");var subQ1=sQuery(id+"F0.wireOp",EDGE,"E123.MirrorCS");var subQ2=sQuery(id+"F0.wireOp",EDGE,"E119.MirrorCS");var subQ3=sQuery(id+"F0.wireOp",EDGE,"E122.MirrorCS");var subQ4=sQuery(id+"F0.wireOp",EDGE,"E115.MirrorCS");var subQ5=sQuery(id+"F0.wireOp",EDGE,"E120.MirrorCS");var subQ6=sQuery(id+"F0.wireOp",EDGE,"E116.MirrorCS");var subQ7=sQuery(id+"F0.wireOp",EDGE,"E117.MirrorCS");var subQ8=sQuery(id+"F0.wireOp",EDGE,"E124.MirrorCS");var subQ9=sQuery(id+"F0.wireOp",EDGE,"E121.MirrorCS");Q0=makeQuery(id+"F5.boolean.opBoolean","SPLIT",FACE,{"disambiguationData":[TD([makeQuery(id+"F1.opExtrude","SWEPT_FACE",FACE,{"disambiguationData":[OSD([subQ4])]})])],"derivedFrom":makeQuery(id+"F1.opExtrude","CAP_FACE",FACE,{"disambiguationData":[OSD([subQ4,subQ6,subQ7,subQ9,subQ5,subQ3,subQ2,subQ1,subQ8,subQ0,sQuery(id+"F0.wireOp",EDGE,"E129.MirrorCS"),sQuery(id+"F0.wireOp",EDGE,"E130.MirrorCS")])],"isStart":false})});}
            var sketch = newSketch(context, id + "F6", { "sketchPlane" : qUnion([Q0])});
            skLineSegment(sketch, "E261", {"start": v(1034.93, 198.47) * mm, "end": v(1034.93, -110.58) * mm});
            skPoint(sketch, "E262.0", {"position": v(916.46, 12.7) * mm});
            skArc(sketch, "E262.1", {"start": v(814.07, 120.65) * mm, "mid": v(899.38, 85.31) * mm, "end": v(934.72, 0) * mm});
            skArc(sketch, "E262.2", {"start": v(814.07, 113.03) * mm, "mid": v(894, 79.92) * mm, "end": v(927.1, 0) * mm});
            skArc(sketch, "E262.3", {"start": v(814.07, 127) * mm, "mid": v(903.87, 89.8) * mm, "end": v(941.07, 0) * mm});
            skLineSegment(sketch, "E262.4", {"start": v(941.07, 0) * mm, "end": v(915.67, 0) * mm});
            skLineSegment(sketch, "E262.5", {"start": v(902.97, 0) * mm, "end": v(877.57, 0) * mm});
            skArc(sketch, "E262.6", {"start": v(902.97, 12.7) * mm, "mid": v(904.35, 6.35) * mm, "end": v(902.97, 0) * mm});
            skArc(sketch, "E262.7", {"start": v(902.97, 12.7) * mm, "mid": v(909.32, 19.05) * mm, "end": v(915.67, 12.7) * mm});
            skArc(sketch, "E262.8", {"start": v(915.67, 12.7) * mm, "mid": v(914.28, 6.35) * mm, "end": v(915.67, 0) * mm});
            skPoint(sketch, "E262.9", {"position": v(886, 12.7) * mm});
            skArc(sketch, "E262.10", {"start": v(814.07, 77.47) * mm, "mid": v(868.85, 54.78) * mm, "end": v(891.54, 0) * mm});
            skArc(sketch, "E262.11", {"start": v(814.07, 69.85) * mm, "mid": v(863.46, 49.4) * mm, "end": v(883.92, 0) * mm});
            skArc(sketch, "E262.12", {"start": v(814.07, 63.5) * mm, "mid": v(858.97, 44.9) * mm, "end": v(877.57, 0) * mm});
            skLineSegment(sketch, "E262.13", {"start": v(814.07, 63.5) * mm, "end": v(814.07, 88.9) * mm});
            skLineSegment(sketch, "E262.14", {"start": v(814.07, 101.6) * mm, "end": v(814.07, 127) * mm});
            skArc(sketch, "E262.15", {"start": v(801.37, 101.6) * mm, "mid": v(807.72, 100.21) * mm, "end": v(814.07, 101.6) * mm});
            skArc(sketch, "E262.16", {"start": v(801.37, 88.9) * mm, "mid": v(807.72, 90.29) * mm, "end": v(814.07, 88.9) * mm});
            skArc(sketch, "E262.17", {"start": v(801.37, 88.9) * mm, "mid": v(795.02, 95.25) * mm, "end": v(801.37, 101.6) * mm});
            skArc(sketch, "E263.MirrorCS", {"start": v(1268.5, 88.9) * mm, "mid": v(1262.14, 90.29) * mm, "end": v(1255.8, 88.9) * mm});
            skArc(sketch, "E264.MirrorCS", {"start": v(1268.5, 101.6) * mm, "mid": v(1262.14, 100.21) * mm, "end": v(1255.8, 101.6) * mm});
            skArc(sketch, "E265.MirrorCS", {"start": v(1154.2, 12.7) * mm, "mid": v(1155.58, 6.35) * mm, "end": v(1154.2, 0) * mm});
            skArc(sketch, "E266.MirrorCS", {"start": v(1268.5, 88.9) * mm, "mid": v(1274.84, 95.25) * mm, "end": v(1268.5, 101.6) * mm});
            skArc(sketch, "E267.MirrorCS", {"start": v(1166.9, 12.7) * mm, "mid": v(1165.5, 6.35) * mm, "end": v(1166.9, 0) * mm});
            skArc(sketch, "E268.MirrorCS", {"start": v(1166.9, 12.7) * mm, "mid": v(1160.54, 19.05) * mm, "end": v(1154.2, 12.7) * mm});
            skLineSegment(sketch, "E269.MirrorCS", {"start": v(1128.8, 0) * mm, "end": v(1154.2, 0) * mm});
            skLineSegment(sketch, "E270.MirrorCS", {"start": v(1255.8, 101.6) * mm, "end": v(1255.8, 127) * mm});
            skLineSegment(sketch, "E271.MirrorCS", {"start": v(1255.8, 63.5) * mm, "end": v(1255.8, 88.9) * mm});
            skLineSegment(sketch, "E272.MirrorCS", {"start": v(1166.9, 0) * mm, "end": v(1192.3, 0) * mm});
            skArc(sketch, "E273.MirrorCS", {"start": v(1255.8, 127) * mm, "mid": v(1166, 89.8) * mm, "end": v(1128.8, 0) * mm});
            skArc(sketch, "E274.MirrorCS", {"start": v(1255.8, 113.03) * mm, "mid": v(1175.87, 79.92) * mm, "end": v(1142.76, 0) * mm});
            skArc(sketch, "E275.MirrorCS", {"start": v(1255.8, 120.65) * mm, "mid": v(1170.48, 85.31) * mm, "end": v(1135.14, 0) * mm});
            skPoint(sketch, "E276.MirrorP", {"position": v(1183.87, 12.7) * mm});
            skPoint(sketch, "E277.MirrorP", {"position": v(1153.4, 12.7) * mm});
            skArc(sketch, "E278.MirrorCS", {"start": v(1255.8, 63.5) * mm, "mid": v(1210.9, 44.9) * mm, "end": v(1192.3, 0) * mm});
            skArc(sketch, "E279.MirrorCS", {"start": v(1255.8, 69.85) * mm, "mid": v(1206.4, 49.4) * mm, "end": v(1185.94, 0) * mm});
            skArc(sketch, "E280.MirrorCS", {"start": v(1255.8, 77.47) * mm, "mid": v(1201.01, 54.78) * mm, "end": v(1178.32, 0) * mm});
            skLineSegment(sketch, "E281", {"start": v(1519.22, 198.47) * mm, "end": v(1519.22, -154.52) * mm});
            skArc(sketch, "E282.MirrorCS", {"start": v(1871.54, 12.7) * mm, "mid": v(1877.9, 19.05) * mm, "end": v(1884.24, 12.7) * mm});
            skLineSegment(sketch, "E283.MirrorCS", {"start": v(1909.64, 0) * mm, "end": v(1884.24, 0) * mm});
            skArc(sketch, "E284.MirrorCS", {"start": v(1884.24, 12.7) * mm, "mid": v(1882.86, 6.35) * mm, "end": v(1884.24, 0) * mm});
            skArc(sketch, "E285.MirrorCS", {"start": v(1871.54, 12.7) * mm, "mid": v(1872.93, 6.35) * mm, "end": v(1871.54, 0) * mm});
            skArc(sketch, "E286.MirrorCS", {"start": v(1769.94, 88.9) * mm, "mid": v(1776.3, 90.29) * mm, "end": v(1782.64, 88.9) * mm});
            skArc(sketch, "E287.MirrorCS", {"start": v(1769.94, 88.9) * mm, "mid": v(1763.6, 95.25) * mm, "end": v(1769.94, 101.6) * mm});
            skArc(sketch, "E288.MirrorCS", {"start": v(1769.94, 101.6) * mm, "mid": v(1776.3, 100.21) * mm, "end": v(1782.64, 101.6) * mm});
            skLineSegment(sketch, "E289.MirrorCS", {"start": v(1782.64, 63.5) * mm, "end": v(1782.64, 88.9) * mm});
            skLineSegment(sketch, "E290.MirrorCS", {"start": v(1782.64, 101.6) * mm, "end": v(1782.64, 127) * mm});
            skLineSegment(sketch, "E291.MirrorCS", {"start": v(1871.54, 0) * mm, "end": v(1846.14, 0) * mm});
            skArc(sketch, "E292.MirrorCS", {"start": v(1782.64, 77.47) * mm, "mid": v(1837.42, 54.78) * mm, "end": v(1860.11, 0) * mm});
            skArc(sketch, "E293.MirrorCS", {"start": v(1782.64, 63.5) * mm, "mid": v(1827.54, 44.9) * mm, "end": v(1846.14, 0) * mm});
            skArc(sketch, "E294.MirrorCS", {"start": v(1782.64, 127) * mm, "mid": v(1872.44, 89.8) * mm, "end": v(1909.64, 0) * mm});
            skArc(sketch, "E295.MirrorCS", {"start": v(1782.64, 120.65) * mm, "mid": v(1867.95, 85.31) * mm, "end": v(1903.3, 0) * mm});
            skPoint(sketch, "E296.MirrorP", {"position": v(1854.57, 12.7) * mm});
            skArc(sketch, "E297.MirrorCS", {"start": v(1782.64, 69.85) * mm, "mid": v(1832.03, 49.4) * mm, "end": v(1852.5, 0) * mm});
            skArc(sketch, "E298.MirrorCS", {"start": v(1782.64, 113.03) * mm, "mid": v(1862.57, 79.92) * mm, "end": v(1895.67, 0) * mm});
            skPoint(sketch, "E299.MirrorP", {"position": v(1885.03, 12.7) * mm});
            skLineSegment(sketch, "E300", {"start": v(2077.79, 229.2) * mm, "end": v(2077.79, -130.23) * mm});
            skArc(sketch, "E301.MirrorCS", {"start": v(2271.33, 12.7) * mm, "mid": v(2272.72, 6.35) * mm, "end": v(2271.33, 0) * mm});
            skArc(sketch, "E302.MirrorCS", {"start": v(2284.03, 12.7) * mm, "mid": v(2277.68, 19.05) * mm, "end": v(2271.33, 12.7) * mm});
            skArc(sketch, "E303.MirrorCS", {"start": v(2284.03, 12.7) * mm, "mid": v(2282.65, 6.35) * mm, "end": v(2284.03, 0) * mm});
            skLineSegment(sketch, "E304.MirrorCS", {"start": v(2372.93, 63.5) * mm, "end": v(2372.93, 88.9) * mm});
            skArc(sketch, "E305.MirrorCS", {"start": v(2385.63, 88.9) * mm, "mid": v(2379.28, 90.29) * mm, "end": v(2372.93, 88.9) * mm});
            skLineSegment(sketch, "E306.MirrorCS", {"start": v(2245.93, 0) * mm, "end": v(2271.33, 0) * mm});
            skArc(sketch, "E307.MirrorCS", {"start": v(2385.63, 101.6) * mm, "mid": v(2379.28, 100.21) * mm, "end": v(2372.93, 101.6) * mm});
            skArc(sketch, "E308.MirrorCS", {"start": v(2385.63, 88.9) * mm, "mid": v(2391.98, 95.25) * mm, "end": v(2385.63, 101.6) * mm});
            skLineSegment(sketch, "E309.MirrorCS", {"start": v(2372.93, 101.6) * mm, "end": v(2372.93, 127) * mm});
            skLineSegment(sketch, "E310.MirrorCS", {"start": v(2284.03, 0) * mm, "end": v(2309.43, 0) * mm});
            skArc(sketch, "E311.MirrorCS", {"start": v(2372.93, 77.47) * mm, "mid": v(2318.15, 54.78) * mm, "end": v(2295.46, 0) * mm});
            skPoint(sketch, "E312.MirrorP", {"position": v(2301, 12.7) * mm});
            skArc(sketch, "E313.MirrorCS", {"start": v(2372.93, 63.5) * mm, "mid": v(2328.03, 44.9) * mm, "end": v(2309.43, 0) * mm});
            skArc(sketch, "E314.MirrorCS", {"start": v(2372.93, 127) * mm, "mid": v(2283.13, 89.8) * mm, "end": v(2245.93, 0) * mm});
            skArc(sketch, "E315.MirrorCS", {"start": v(2372.93, 120.65) * mm, "mid": v(2287.62, 85.31) * mm, "end": v(2252.28, 0) * mm});
            skArc(sketch, "E316.MirrorCS", {"start": v(2372.93, 69.85) * mm, "mid": v(2323.54, 49.4) * mm, "end": v(2303.08, 0) * mm});
            skPoint(sketch, "E317.MirrorP", {"position": v(2270.54, 12.7) * mm});
            skArc(sketch, "E318.MirrorCS", {"start": v(2372.93, 113.03) * mm, "mid": v(2293, 79.92) * mm, "end": v(2259.9, 0) * mm});
            skLineSegment(sketch, "E319", {"start": v(2590.29, 330.34) * mm, "end": v(2590.29, -152.83) * mm});
            skArc(sketch, "E320.MirrorCS", {"start": v(2896.54, 12.7) * mm, "mid": v(2902.89, 19.05) * mm, "end": v(2909.24, 12.7) * mm});
            skLineSegment(sketch, "E321.MirrorCS", {"start": v(2896.54, 0) * mm, "end": v(2871.14, 0) * mm});
            skArc(sketch, "E322.MirrorCS", {"start": v(2909.24, 12.7) * mm, "mid": v(2907.85, 6.35) * mm, "end": v(2909.24, 0) * mm});
            skArc(sketch, "E323.MirrorCS", {"start": v(2896.54, 12.7) * mm, "mid": v(2897.92, 6.35) * mm, "end": v(2896.54, 0) * mm});
            skLineSegment(sketch, "E324.MirrorCS", {"start": v(2934.64, 0) * mm, "end": v(2909.24, 0) * mm});
            skLineSegment(sketch, "E325.MirrorCS", {"start": v(2807.64, 63.5) * mm, "end": v(2807.64, 88.9) * mm});
            skArc(sketch, "E326.MirrorCS", {"start": v(2794.94, 101.6) * mm, "mid": v(2801.29, 100.21) * mm, "end": v(2807.64, 101.6) * mm});
            skArc(sketch, "E327.MirrorCS", {"start": v(2794.94, 88.9) * mm, "mid": v(2801.29, 90.29) * mm, "end": v(2807.64, 88.9) * mm});
            skArc(sketch, "E328.MirrorCS", {"start": v(2794.94, 88.9) * mm, "mid": v(2788.59, 95.25) * mm, "end": v(2794.94, 101.6) * mm});
            skLineSegment(sketch, "E329.MirrorCS", {"start": v(2807.64, 101.6) * mm, "end": v(2807.64, 127) * mm});
            skArc(sketch, "E330.MirrorCS", {"start": v(2807.64, 63.5) * mm, "mid": v(2852.54, 44.9) * mm, "end": v(2871.14, 0) * mm});
            skArc(sketch, "E331.MirrorCS", {"start": v(2807.64, 120.65) * mm, "mid": v(2892.95, 85.31) * mm, "end": v(2928.29, 0) * mm});
            skPoint(sketch, "E332.MirrorP", {"position": v(2910.03, 12.7) * mm});
            skArc(sketch, "E333.MirrorCS", {"start": v(2807.64, 113.03) * mm, "mid": v(2887.56, 79.92) * mm, "end": v(2920.67, 0) * mm});
            skArc(sketch, "E334.MirrorCS", {"start": v(2807.64, 77.47) * mm, "mid": v(2862.42, 54.78) * mm, "end": v(2885.1, 0) * mm});
            skArc(sketch, "E335.MirrorCS", {"start": v(2807.64, 127) * mm, "mid": v(2897.44, 89.8) * mm, "end": v(2934.64, 0) * mm});
            skArc(sketch, "E336.MirrorCS", {"start": v(2807.64, 69.85) * mm, "mid": v(2857.03, 49.4) * mm, "end": v(2877.49, 0) * mm});
            skPoint(sketch, "E337.MirrorP", {"position": v(2879.57, 12.7) * mm});
            skLineSegment(sketch, "E338", {"start": v(1782.64, 120.65) * mm, "end": v(1782.64, 113.03) * mm});
            skLineSegment(sketch, "E339", {"start": v(1782.64, 69.85) * mm, "end": v(1782.64, 77.47) * mm});
            skLineSegment(sketch, "E340", {"start": v(1852.5, 0) * mm, "end": v(1860.11, 0) * mm});
            skLineSegment(sketch, "E341", {"start": v(1895.67, 0) * mm, "end": v(1903.3, 0) * mm});
            skLineSegment(sketch, "E342", {"start": v(2928.29, 0) * mm, "end": v(2920.67, 0) * mm});
            skLineSegment(sketch, "E343", {"start": v(2885.1, 0) * mm, "end": v(2877.49, 0) * mm});
            skLineSegment(sketch, "E344", {"start": v(2807.64, 77.47) * mm, "end": v(2807.64, 69.85) * mm});
            skLineSegment(sketch, "E345", {"start": v(2807.64, 120.65) * mm, "end": v(2807.64, 113.03) * mm});
            skSolve(sketch);
        }
        {
            var Q0;
            {var subQ8=sQuery(id+"F6.wireOp",EDGE,"E284.MirrorCS");Q0=makeQuery(id+"F6.imprint","IMPRINT",FACE,{"disambiguationData":[TD([[makeQuery(id+"F6.imprint","IMPRINT",EDGE,{"derivedFrom":subQ8}),1.0]])]});}
            var Q1;
            {var subQ0=sQuery(id+"F6.wireOp",EDGE,"E294.MirrorCS");Q1=makeQuery(id+"F6.imprint","IMPRINT",FACE,{"disambiguationData":[TD([[makeQuery(id+"F6.imprint","IMPRINT",EDGE,{"derivedFrom":subQ0}),-1.0]])]});}
            var Q2;
            {var subQ0=sQuery(id+"F6.wireOp",EDGE,"E295.MirrorCS");Q2=makeQuery(id+"F6.imprint","IMPRINT",FACE,{"disambiguationData":[TD([[makeQuery(id+"F6.imprint","IMPRINT",EDGE,{"derivedFrom":subQ0}),-1.0]])]});}
            var Q3;
            {var subQ0=sQuery(id+"F6.wireOp",EDGE,"E297.MirrorCS");Q3=makeQuery(id+"F6.imprint","IMPRINT",FACE,{"disambiguationData":[TD([[makeQuery(id+"F6.imprint","IMPRINT",EDGE,{"derivedFrom":subQ0}),1.0]])]});}
            var Q4;
            {var subQ2=sQuery(id+"F6.wireOp",EDGE,"E297.MirrorCS");Q4=makeQuery(id+"F6.imprint","IMPRINT",FACE,{"disambiguationData":[TD([[makeQuery(id+"F6.imprint","IMPRINT",EDGE,{"derivedFrom":subQ2}),-1.0]])]});}
            var Q5;
            Q5=makeQuery(id+"F6.imprint","IMPRINT",FACE,{"disambiguationData":[TD([[makeQuery(id+"F6.imprint","IMPRINT",EDGE,{"derivedFrom":sQuery(id+"F6.wireOp",EDGE,"E320.MirrorCS")}),1.0]])]});
            var Q6;
            {var subQ0=sQuery(id+"F6.wireOp",EDGE,"E336.MirrorCS");Q6=makeQuery(id+"F6.imprint","IMPRINT",FACE,{"disambiguationData":[TD([[makeQuery(id+"F6.imprint","IMPRINT",EDGE,{"derivedFrom":subQ0}),1.0]])]});}
            var Q7;
            {var subQ0=sQuery(id+"F6.wireOp",EDGE,"E330.MirrorCS");Q7=makeQuery(id+"F6.imprint","IMPRINT",FACE,{"disambiguationData":[TD([[makeQuery(id+"F6.imprint","IMPRINT",EDGE,{"derivedFrom":subQ0}),1.0]])]});}
            var Q8;
            {var subQ2=sQuery(id+"F6.wireOp",EDGE,"E331.MirrorCS");Q8=makeQuery(id+"F6.imprint","IMPRINT",FACE,{"disambiguationData":[TD([[makeQuery(id+"F6.imprint","IMPRINT",EDGE,{"derivedFrom":subQ2}),1.0]])]});}
            var Q9;
            {var subQ0=sQuery(id+"F6.wireOp",EDGE,"E331.MirrorCS");Q9=makeQuery(id+"F6.imprint","IMPRINT",FACE,{"disambiguationData":[TD([[makeQuery(id+"F6.imprint","IMPRINT",EDGE,{"derivedFrom":subQ0}),-1.0]])]});}
            var Q10;
            {var subQ5=sQuery(id+"F6.wireOp",EDGE,"E265.MirrorCS");Q10=makeQuery(id+"F6.imprint","IMPRINT",FACE,{"disambiguationData":[TD([[makeQuery(id+"F6.imprint","IMPRINT",EDGE,{"derivedFrom":subQ5}),-1.0]])]});}
            var Q11;
            {var subQ0=sQuery(id+"F6.wireOp",EDGE,"E273.MirrorCS");Q11=makeQuery(id+"F6.imprint","IMPRINT",FACE,{"disambiguationData":[TD([[makeQuery(id+"F6.imprint","IMPRINT",EDGE,{"derivedFrom":subQ0}),1.0]])]});}
            var Q12;
            {var subQ2=sQuery(id+"F6.wireOp",EDGE,"E279.MirrorCS");Q12=makeQuery(id+"F6.imprint","IMPRINT",FACE,{"disambiguationData":[TD([[makeQuery(id+"F6.imprint","IMPRINT",EDGE,{"derivedFrom":subQ2}),1.0]])]});}
            extrude(context, id + "F7", {"entities" : qUnion([Q0, Q1, Q2, Q3, Q4, Q5, Q6, Q7, Q8, Q9, Q10, Q11, Q12]), "depth" : 6.35 * mm});
        }
        {
            var Q0;
            Q0=makeQuery(id+"F7.opExtrude","CAP_FACE",FACE,{"disambiguationData":[OSD([sQuery(id+"F6.wireOp",EDGE,"E284.MirrorCS"),sQuery(id+"F6.wireOp",EDGE,"E285.MirrorCS"),sQuery(id+"F6.wireOp",EDGE,"E282.MirrorCS"),sQuery(id+"F6.wireOp",EDGE,"E283.MirrorCS"),sQuery(id+"F6.wireOp",EDGE,"E288.MirrorCS"),sQuery(id+"F6.wireOp",EDGE,"E286.MirrorCS"),sQuery(id+"F6.wireOp",EDGE,"E287.MirrorCS"),sQuery(id+"F6.wireOp",EDGE,"E290.MirrorCS"),sQuery(id+"F6.wireOp",EDGE,"E289.MirrorCS"),sQuery(id+"F6.wireOp",EDGE,"E291.MirrorCS"),sQuery(id+"F6.wireOp",EDGE,"E294.MirrorCS"),sQuery(id+"F6.wireOp",EDGE,"E293.MirrorCS"),sQuery(id+"F6.wireOp",EDGE,"E339"),sQuery(id+"F6.wireOp",EDGE,"E340"),sQuery(id+"F6.wireOp",EDGE,"E341"),sQuery(id+"F6.wireOp",EDGE,"E338")])],"isStart":false});
            var sketch = newSketch(context, id + "F8", { "sketchPlane" : qUnion([Q0])});
            skArc(sketch, "E346.0", {"start": v(2807.64, 120.65) * mm, "mid": v(2892.95, 85.31) * mm, "end": v(2928.29, 0) * mm});
            skArc(sketch, "E346.1", {"start": v(2807.64, 113.03) * mm, "mid": v(2887.56, 79.92) * mm, "end": v(2920.67, 0) * mm});
            skArc(sketch, "E346.2", {"start": v(2807.64, 77.47) * mm, "mid": v(2862.42, 54.78) * mm, "end": v(2885.1, 0) * mm});
            skArc(sketch, "E346.3", {"start": v(2807.64, 69.85) * mm, "mid": v(2857.03, 49.4) * mm, "end": v(2877.49, 0) * mm});
            skLineSegment(sketch, "E346.4", {"start": v(2807.64, 69.85) * mm, "end": v(2807.64, 77.47) * mm});
            skLineSegment(sketch, "E346.5", {"start": v(2807.64, 113.03) * mm, "end": v(2807.64, 120.65) * mm});
            skLineSegment(sketch, "E346.6", {"start": v(2928.29, 0) * mm, "end": v(2920.67, 0) * mm});
            skLineSegment(sketch, "E346.7", {"start": v(2885.1, 0) * mm, "end": v(2877.49, 0) * mm});
            skPoint(sketch, "E347.orphan", {"position": v(2807.64, 127) * mm});
            skPoint(sketch, "E348.orphan", {"position": v(2807.64, 101.6) * mm});
            skPoint(sketch, "E349.orphan", {"position": v(2807.64, 88.9) * mm});
            skPoint(sketch, "E350.orphan", {"position": v(2807.64, 63.5) * mm});
            skPoint(sketch, "E351.orphan", {"position": v(2909.24, 0) * mm});
            skPoint(sketch, "E352.orphan", {"position": v(2934.64, 0) * mm});
            skPoint(sketch, "E353.orphan", {"position": v(2896.54, 0) * mm});
            skPoint(sketch, "E354.orphan", {"position": v(2871.14, 0) * mm});
            skArc(sketch, "E355.0", {"start": v(1782.64, 120.65) * mm, "mid": v(1867.95, 85.31) * mm, "end": v(1903.3, 0) * mm});
            skArc(sketch, "E355.1", {"start": v(1782.64, 113.03) * mm, "mid": v(1862.57, 79.92) * mm, "end": v(1895.67, 0) * mm});
            skArc(sketch, "E355.2", {"start": v(1782.64, 69.85) * mm, "mid": v(1832.03, 49.4) * mm, "end": v(1852.5, 0) * mm});
            skArc(sketch, "E355.3", {"start": v(1782.64, 77.47) * mm, "mid": v(1837.42, 54.78) * mm, "end": v(1860.11, 0) * mm});
            skLineSegment(sketch, "E355.4", {"start": v(1860.11, 0) * mm, "end": v(1852.5, 0) * mm});
            skLineSegment(sketch, "E355.5", {"start": v(1903.3, 0) * mm, "end": v(1895.67, 0) * mm});
            skLineSegment(sketch, "E355.6", {"start": v(1782.64, 113.03) * mm, "end": v(1782.64, 120.65) * mm});
            skLineSegment(sketch, "E355.7", {"start": v(1782.64, 69.85) * mm, "end": v(1782.64, 77.47) * mm});
            skPoint(sketch, "E356.orphan", {"position": v(1782.64, 127) * mm});
            skPoint(sketch, "E357.orphan", {"position": v(1909.64, 0) * mm});
            skPoint(sketch, "E358.orphan", {"position": v(1884.24, 0) * mm});
            skPoint(sketch, "E359.orphan", {"position": v(1782.64, 101.6) * mm});
            skPoint(sketch, "E360.orphan", {"position": v(1782.64, 88.9) * mm});
            skPoint(sketch, "E361.orphan", {"position": v(1871.54, 0) * mm});
            skPoint(sketch, "E362.orphan", {"position": v(1846.14, 0) * mm});
            skPoint(sketch, "E363.orphan", {"position": v(1782.64, 63.5) * mm});
            skSolve(sketch);
        }
        {
            var Q0;
            Q0=makeQuery(id+"F8.imprint","IMPRINT",FACE,{"disambiguationData":[TD([[makeQuery(id+"F8.imprint","IMPRINT",EDGE,{"derivedFrom":sQuery(id+"F8.wireOp",EDGE,"E355.0")}),-1.0]])]});
            var Q1;
            Q1=makeQuery(id+"F8.imprint","IMPRINT",FACE,{"disambiguationData":[TD([[makeQuery(id+"F8.imprint","IMPRINT",EDGE,{"derivedFrom":sQuery(id+"F8.wireOp",EDGE,"E355.2")}),1.0]])]});
            var Q2;
            Q2=makeQuery(id+"F8.imprint","IMPRINT",FACE,{"disambiguationData":[TD([[makeQuery(id+"F8.imprint","IMPRINT",EDGE,{"derivedFrom":sQuery(id+"F8.wireOp",EDGE,"E346.2")}),-1.0]])]});
            var Q3;
            Q3=makeQuery(id+"F8.imprint","IMPRINT",FACE,{"disambiguationData":[TD([[makeQuery(id+"F8.imprint","IMPRINT",EDGE,{"derivedFrom":sQuery(id+"F8.wireOp",EDGE,"E346.0")}),-1.0]])]});
            extrude(context, id + "F9", {"entities" : qUnion([Q0, Q1, Q2, Q3]), "operationType" : NewBodyOperationType.REMOVE, "oppositeDirection" : true, "depth" : 1.9 * mm});
        }
        {
            var Q0;
            {var subQ0=sQuery(id+"F6.wireOp",EDGE,"E274.MirrorCS");Q0=makeQuery(id+"F6.imprint","IMPRINT",FACE,{"disambiguationData":[TD([[makeQuery(id+"F6.imprint","IMPRINT",EDGE,{"derivedFrom":subQ0}),-1.0]])]});}
            var Q1;
            {var subQ0=sQuery(id+"F6.wireOp",EDGE,"E280.MirrorCS");Q1=makeQuery(id+"F6.imprint","IMPRINT",FACE,{"disambiguationData":[TD([[makeQuery(id+"F6.imprint","IMPRINT",EDGE,{"derivedFrom":subQ0}),1.0]])]});}
            extrude(context, id + "F10", {"entities" : qUnion([Q0, Q1]), "operationType" : NewBodyOperationType.ADD, "depth" : 4.44 * mm});
        }
        {
            var Q0;
            Q0=makeQuery(id+"F1.opExtrude","SWEPT_BODY",BODY,{"disambiguationData":[OSD([sQuery(id+"F0.wireOp",EDGE,"E133.MirrorCS"),sQuery(id+"F0.wireOp",EDGE,"E135.MirrorCS"),sQuery(id+"F0.wireOp",EDGE,"E138.MirrorCS"),sQuery(id+"F0.wireOp",EDGE,"E134.MirrorCS"),sQuery(id+"F0.wireOp",EDGE,"E137.MirrorCS"),sQuery(id+"F0.wireOp",EDGE,"E139.MirrorCS"),sQuery(id+"F0.wireOp",EDGE,"E140.MirrorCS"),sQuery(id+"F0.wireOp",EDGE,"E141.MirrorCS"),sQuery(id+"F0.wireOp",EDGE,"E143.MirrorCS"),sQuery(id+"F0.wireOp",EDGE,"E144.MirrorCS"),sQuery(id+"F0.wireOp",EDGE,"E146.MirrorCS"),sQuery(id+"F0.wireOp",EDGE,"E147.MirrorCS")])]});
            var Q1;
            Q1=makeQuery(id+"F7.opExtrude","SWEPT_BODY",BODY,{"disambiguationData":[OSD([sQuery(id+"F6.wireOp",EDGE,"E265.MirrorCS"),sQuery(id+"F6.wireOp",EDGE,"E268.MirrorCS"),sQuery(id+"F6.wireOp",EDGE,"E267.MirrorCS"),sQuery(id+"F6.wireOp",EDGE,"E263.MirrorCS"),sQuery(id+"F6.wireOp",EDGE,"E266.MirrorCS"),sQuery(id+"F6.wireOp",EDGE,"E264.MirrorCS"),sQuery(id+"F6.wireOp",EDGE,"E271.MirrorCS"),sQuery(id+"F6.wireOp",EDGE,"E272.MirrorCS"),sQuery(id+"F6.wireOp",EDGE,"E269.MirrorCS"),sQuery(id+"F6.wireOp",EDGE,"E270.MirrorCS"),sQuery(id+"F6.wireOp",EDGE,"E274.MirrorCS"),sQuery(id+"F6.wireOp",EDGE,"E280.MirrorCS")])]});
            deleteBodies(context, id + "F11", {"entities" : qUnion([Q0, Q1])});
        }
        {
            var Q0;
            Q0=makeQuery(id+"F7.opExtrude","SWEPT_BODY",BODY,{"disambiguationData":[OSD([sQuery(id+"F6.wireOp",EDGE,"E320.MirrorCS"),sQuery(id+"F6.wireOp",EDGE,"E321.MirrorCS"),sQuery(id+"F6.wireOp",EDGE,"E322.MirrorCS"),sQuery(id+"F6.wireOp",EDGE,"E323.MirrorCS"),sQuery(id+"F6.wireOp",EDGE,"E324.MirrorCS"),sQuery(id+"F6.wireOp",EDGE,"E325.MirrorCS"),sQuery(id+"F6.wireOp",EDGE,"E327.MirrorCS"),sQuery(id+"F6.wireOp",EDGE,"E326.MirrorCS"),sQuery(id+"F6.wireOp",EDGE,"E328.MirrorCS"),sQuery(id+"F6.wireOp",EDGE,"E329.MirrorCS"),sQuery(id+"F6.wireOp",EDGE,"E330.MirrorCS"),sQuery(id+"F6.wireOp",EDGE,"E335.MirrorCS"),sQuery(id+"F6.wireOp",EDGE,"E342"),sQuery(id+"F6.wireOp",EDGE,"E343"),sQuery(id+"F6.wireOp",EDGE,"E344"),sQuery(id+"F6.wireOp",EDGE,"E345")])]});
            deleteBodies(context, id + "F12", {"entities" : qUnion([Q0])});
        }
    });
